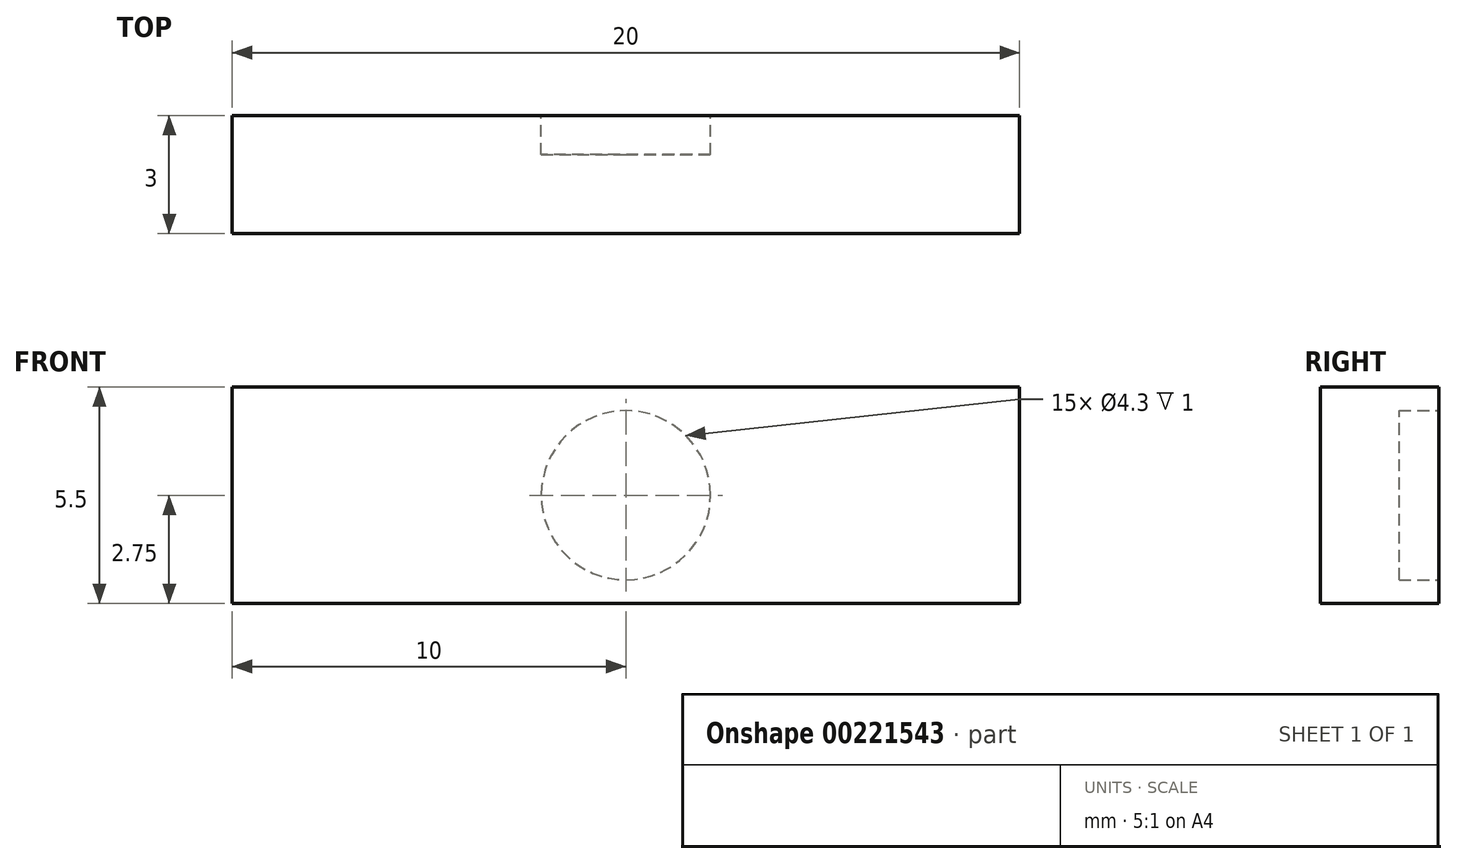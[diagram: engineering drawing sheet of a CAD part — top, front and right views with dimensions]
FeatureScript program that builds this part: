
annotation { "Feature Type Name" : "Feature", "Feature Type Description" : "" }
export const myFeature = defineFeature(function(context is Context, id is Id, definition is map)
    precondition{}
    {
        {
            var Q0;
            Q0=qCreatedBy(makeId("Front.planeOp"),FACE);
            var sketch = newSketch(context, id + "F0", { "sketchPlane" : qUnion([Q0])});
            skLineSegment(sketch, "E0.bottom", {"start": v(-10, 2.75) * mm, "end": v(10, 2.75) * mm});
            skLineSegment(sketch, "E0.top", {"start": v(-10, -2.75) * mm, "end": v(10, -2.75) * mm});
            skLineSegment(sketch, "E0.left", {"start": v(-10, 2.75) * mm, "end": v(-10, -2.75) * mm});
            skLineSegment(sketch, "E0.right", {"start": v(10, 2.75) * mm, "end": v(10, -2.75) * mm});
            skPoint(sketch, "E0.middle", {"position": v(0, 0) * mm});
            skCircle(sketch, "E1", {"center": v(0, 0) * mm, "radius": 2.15 * mm});
            skSolve(sketch);
        }
        {
            var Q0;
            Q0=makeQuery(id+"F0.imprint","IMPRINT",FACE,{"disambiguationData":[TD([[makeQuery(id+"F0.imprint","IMPRINT",EDGE,{"derivedFrom":sQuery(id+"F0.wireOp",EDGE,"E0.bottom")}),-1.0]])]});
            var Q1;
            Q1=makeQuery(id+"F0.imprint","IMPRINT",FACE,{"disambiguationData":[TD([[makeQuery(id+"F0.imprint","IMPRINT",EDGE,{"derivedFrom":sQuery(id+"F0.wireOp",EDGE,"E1")}),1.0]])]});
            extrude(context, id + "F1", {"entities" : qUnion([Q0, Q1]), "depth" : 3 * mm});
        }
        {
            var Q0;
            Q0=makeQuery(id+"F0.imprint","IMPRINT",FACE,{"disambiguationData":[TD([[makeQuery(id+"F0.imprint","IMPRINT",EDGE,{"derivedFrom":sQuery(id+"F0.wireOp",EDGE,"E1")}),1.0]])]});
            extrude(context, id + "F2", {"entities" : qUnion([Q0]), "operationType" : NewBodyOperationType.REMOVE, "depth" : 1 * mm});
        }
    });
